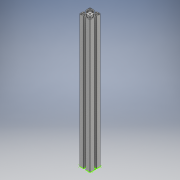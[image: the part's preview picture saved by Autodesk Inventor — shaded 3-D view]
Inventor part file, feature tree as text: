
AUTODESK INVENTOR PART (.ipt)
format: ipt  version: 2018.3 (Build 223284000, 284)  size: 315,392 bytes
history: native  units: mm
features: extrude x1, sketch x1
ambient origin geometry x8: Origin, YZ Plane, XZ Plane, XY Plane, X Axis, Y Axis, Z Axis, Center Point
bodies: Body1 (feature_tree)
feature tree (2):
  extrude  "Extrusión1"  [1 undecoded]
  sketch  "Boceto1"  dims[d0=500.0mm d1=0.0mm]
note: 1 required parameter value undecoded (feature->parameter linkage not recoverable at this tier; creation-order binding heuristic only, values carry confidence <= 0.55)
